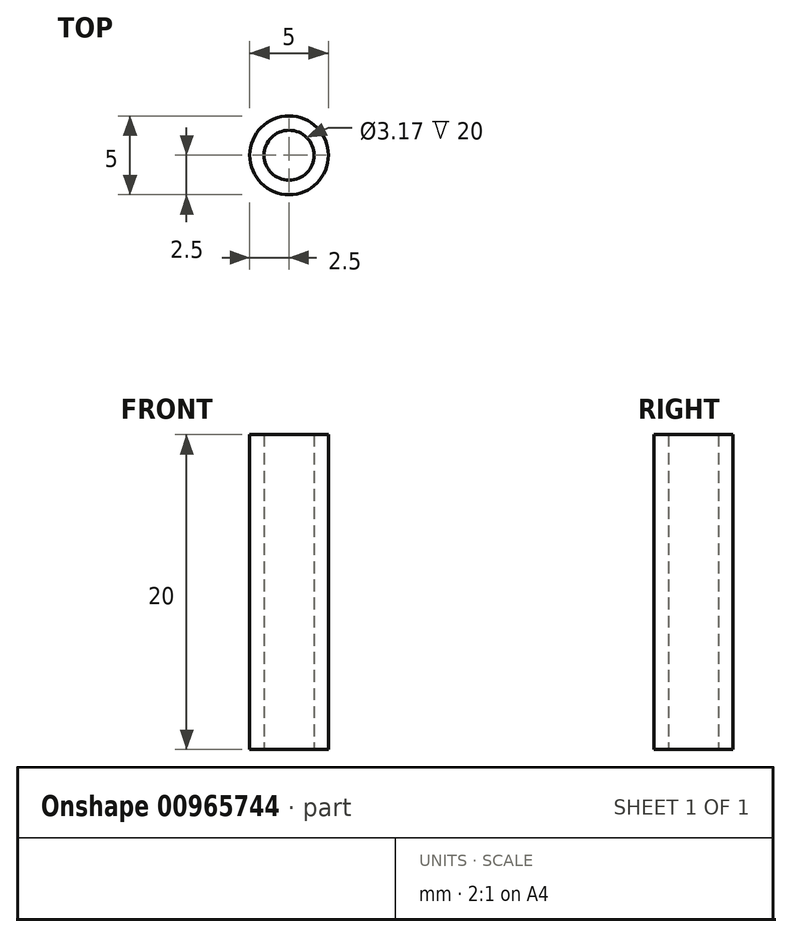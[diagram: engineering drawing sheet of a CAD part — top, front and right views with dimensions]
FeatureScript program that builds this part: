
annotation { "Feature Type Name" : "Feature", "Feature Type Description" : "" }
export const myFeature = defineFeature(function(context is Context, id is Id, definition is map)
    precondition{}
    {
        {
            var Q0;
            Q0=qCreatedBy(makeId("Top.planeOp"),FACE);
            var sketch = newSketch(context, id + "F0", { "sketchPlane" : qUnion([Q0])});
            skCircle(sketch, "E0", {"center": v(0, 0) * mm, "radius": 1.59 * mm});
            skCircle(sketch, "E1", {"center": v(0, 0) * mm, "radius": 2.5 * mm});
            skSolve(sketch);
        }
        {
            var Q0;
            Q0=makeQuery(id+"F0.imprint","IMPRINT",FACE,{"disambiguationData":[TD([[makeQuery(id+"F0.imprint","IMPRINT",EDGE,{"derivedFrom":sQuery(id+"F0.wireOp",EDGE,"E0")}),-1.0]])]});
            extrude(context, id + "F1", {"entities" : qUnion([Q0]), "endBound" : BoundingType.SYMMETRIC, "depth" : 20 * mm, "offsetDistance" : 25 * mm});
        }
    });
